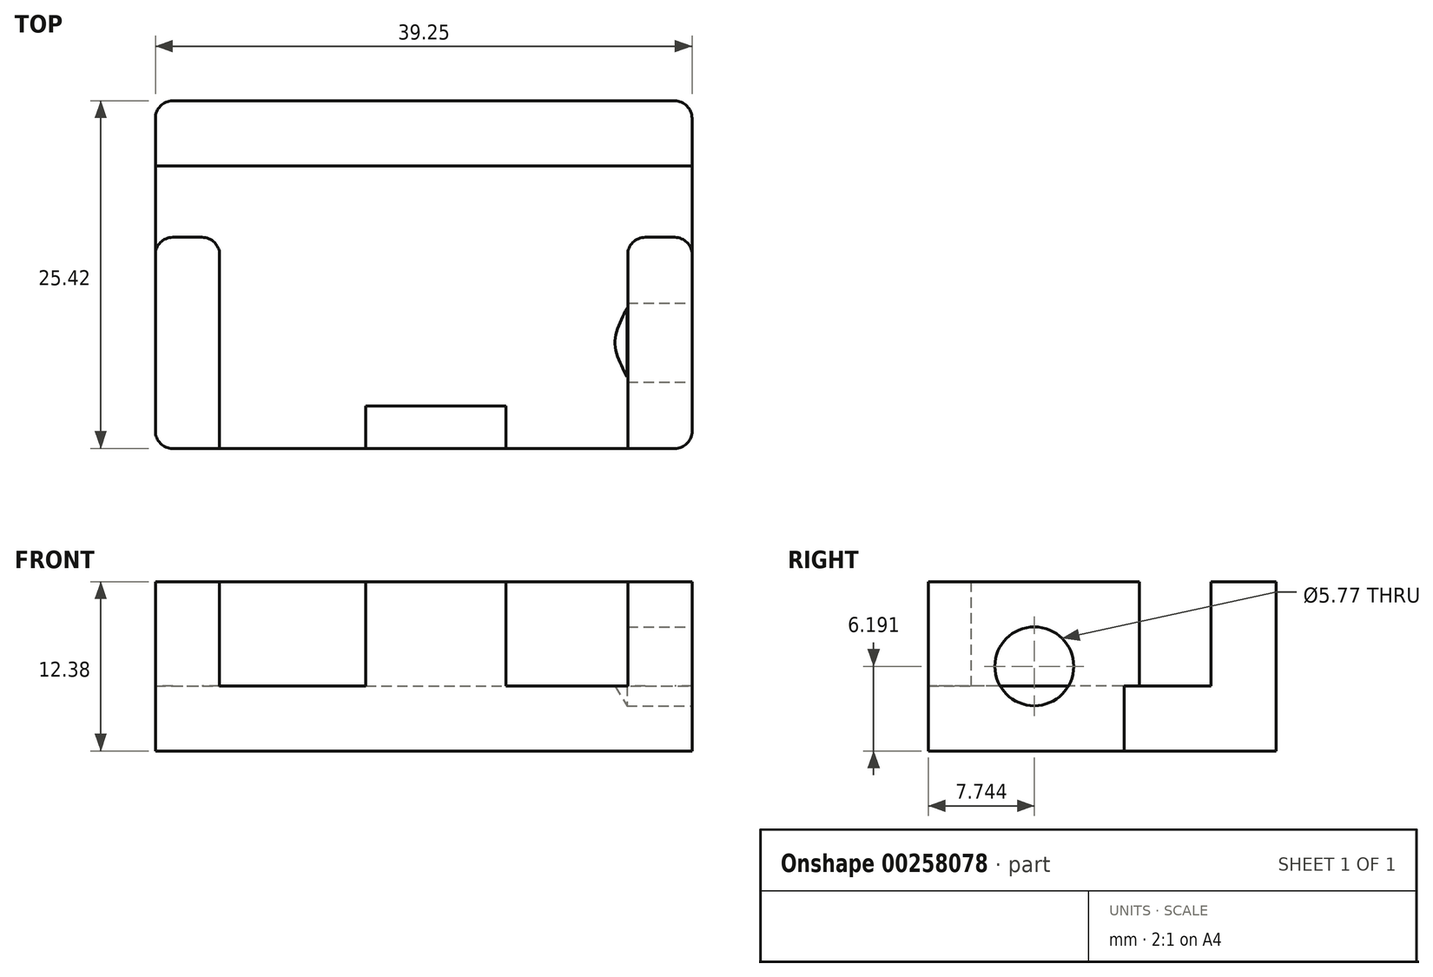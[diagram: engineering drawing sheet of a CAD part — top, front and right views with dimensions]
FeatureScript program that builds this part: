
annotation { "Feature Type Name" : "Feature", "Feature Type Description" : "" }
export const myFeature = defineFeature(function(context is Context, id is Id, definition is map)
    precondition{}
    {
        {
            var Q0;
            Q0=qCreatedBy(makeId("Top.planeOp"),FACE);
            var sketch = newSketch(context, id + "F0", { "sketchPlane" : qUnion([Q0])});
            skLineSegment(sketch, "E0.bottom", {"start": v(19.62, 12.71) * mm, "end": v(-19.62, 12.71) * mm});
            skLineSegment(sketch, "E0.top", {"start": v(19.62, -12.71) * mm, "end": v(-19.62, -12.71) * mm});
            skLineSegment(sketch, "E0.left", {"start": v(19.62, 12.71) * mm, "end": v(19.62, -12.71) * mm});
            skLineSegment(sketch, "E0.right", {"start": v(-19.62, 12.71) * mm, "end": v(-19.62, -12.71) * mm});
            skPoint(sketch, "E0.middle", {"position": v(0, 0) * mm});
            skSolve(sketch);
        }
        {
            var Q0;
            Q0=makeQuery(id+"F0.imprint","IMPRINT",FACE,{"disambiguationData":[TD([[makeQuery(id+"F0.imprint","IMPRINT",EDGE,{"derivedFrom":sQuery(id+"F0.wireOp",EDGE,"E0.bottom")}),1.0]])]});
            extrude(context, id + "F1", {"entities" : qUnion([Q0]), "depth" : 4.76 * mm});
        }
        {
            var Q0;
            Q0=makeQuery(id+"F1.opExtrude","CAP_FACE",FACE,{"disambiguationData":[OSD([sQuery(id+"F0.wireOp",EDGE,"E0.bottom"),sQuery(id+"F0.wireOp",EDGE,"E0.top"),sQuery(id+"F0.wireOp",EDGE,"E0.left"),sQuery(id+"F0.wireOp",EDGE,"E0.right")])],"isStart":false});
            var sketch = newSketch(context, id + "F2", { "sketchPlane" : qUnion([Q0])});
            skLineSegment(sketch, "E1.bottom", {"start": v(-19.62, 2.73) * mm, "end": v(-14.93, 2.73) * mm});
            skLineSegment(sketch, "E1.top", {"start": v(-19.62, -12.71) * mm, "end": v(-14.93, -12.71) * mm});
            skLineSegment(sketch, "E1.left", {"start": v(-19.62, 2.73) * mm, "end": v(-19.62, -12.71) * mm});
            skLineSegment(sketch, "E1.right", {"start": v(-14.93, 2.73) * mm, "end": v(-14.93, -12.71) * mm});
            skLineSegment(sketch, "E2.bottom", {"start": v(-19.62, 12.71) * mm, "end": v(19.62, 12.71) * mm});
            skLineSegment(sketch, "E2.top", {"start": v(-19.62, 7.95) * mm, "end": v(19.62, 7.95) * mm});
            skLineSegment(sketch, "E2.left", {"start": v(-19.62, 12.71) * mm, "end": v(-19.62, 7.95) * mm});
            skLineSegment(sketch, "E2.right", {"start": v(19.62, 12.71) * mm, "end": v(19.62, 7.95) * mm});
            skLineSegment(sketch, "E3.bottom", {"start": v(14.93, 2.73) * mm, "end": v(19.62, 2.73) * mm});
            skLineSegment(sketch, "E3.top", {"start": v(14.93, -12.71) * mm, "end": v(19.62, -12.71) * mm});
            skLineSegment(sketch, "E3.left", {"start": v(14.93, 2.73) * mm, "end": v(14.93, -12.71) * mm});
            skLineSegment(sketch, "E3.right", {"start": v(19.62, 2.73) * mm, "end": v(19.62, -12.71) * mm});
            skLineSegment(sketch, "E4.bottom", {"start": v(-4.23, -12.71) * mm, "end": v(6.01, -12.71) * mm});
            skLineSegment(sketch, "E4.top", {"start": v(-4.23, -9.6) * mm, "end": v(6.01, -9.6) * mm});
            skLineSegment(sketch, "E4.left", {"start": v(-4.23, -12.71) * mm, "end": v(-4.23, -9.6) * mm});
            skLineSegment(sketch, "E4.right", {"start": v(6.01, -12.71) * mm, "end": v(6.01, -9.6) * mm});
            skSolve(sketch);
        }
        {
            var Q0;
            Q0=makeQuery(id+"F2.imprint","IMPRINT",FACE,{"disambiguationData":[TD([[makeQuery(id+"F2.imprint","IMPRINT",EDGE,{"derivedFrom":sQuery(id+"F2.wireOp",EDGE,"E1.bottom")}),-1.0]])]});
            var Q1;
            Q1=makeQuery(id+"F2.imprint","IMPRINT",FACE,{"disambiguationData":[TD([[makeQuery(id+"F2.imprint","IMPRINT",EDGE,{"derivedFrom":sQuery(id+"F2.wireOp",EDGE,"E3.bottom")}),-1.0]])]});
            var Q2;
            Q2=makeQuery(id+"F2.imprint","IMPRINT",FACE,{"disambiguationData":[TD([[makeQuery(id+"F2.imprint","IMPRINT",EDGE,{"derivedFrom":sQuery(id+"F2.wireOp",EDGE,"E4.bottom")}),-1.0]])]});
            var Q3;
            Q3=makeQuery(id+"F2.imprint","IMPRINT",FACE,{"disambiguationData":[TD([[makeQuery(id+"F2.imprint","IMPRINT",EDGE,{"derivedFrom":sQuery(id+"F2.wireOp",EDGE,"E2.bottom")}),1.0]])]});
            extrude(context, id + "F3", {"entities" : qUnion([Q0, Q1, Q2, Q3]), "operationType" : NewBodyOperationType.ADD, "depth" : 7.62 * mm});
        }
        {
            var Q0;
            Q0=makeQuery(id+"F3.boolean.opBoolean","MERGE",FACE,{"derivedFrom":[makeQuery(id+"F1.opExtrude","SWEPT_FACE",FACE,{"disambiguationData":[OSD([sQuery(id+"F0.wireOp",EDGE,"E0.left")])]}),makeQuery(id+"F3.opExtrude","SWEPT_FACE",FACE,{"disambiguationData":[OSD([sQuery(id+"F2.wireOp",EDGE,"E2.right")])]}),makeQuery(id+"F3.opExtrude","SWEPT_FACE",FACE,{"disambiguationData":[OSD([sQuery(id+"F2.wireOp",EDGE,"E3.right")])]})]});
            var sketch = newSketch(context, id + "F4", { "sketchPlane" : qUnion([Q0])});
            skLineSegment(sketch, "E5.bottom", {"start": v(2.73, 12.38) * mm, "end": v(-12.71, 12.38) * mm});
            skLineSegment(sketch, "E5.top", {"start": v(2.73, 0) * mm, "end": v(-12.71, 0) * mm});
            skLineSegment(sketch, "E5.left", {"start": v(2.73, 12.38) * mm, "end": v(2.73, 0) * mm});
            skLineSegment(sketch, "E5.right", {"start": v(-12.71, 12.38) * mm, "end": v(-12.71, 0) * mm});
            skSolve(sketch);
        }
        {
            var Q0;
            {var subQ4=sQuery(id+"F4.wireOp",EDGE,"E5.bottom");Q0=makeQuery(id+"F4.imprint","IMPRINT",FACE,{"disambiguationData":[TD([[makeQuery(id+"F4.imprint","IMPRINT",EDGE,{"derivedFrom":subQ4}),1.0]])]});}
            extrude(context, id + "F5", {"entities" : qUnion([Q0]), "operationType" : NewBodyOperationType.ADD, "depth" : 3 / 406.4 * mm});
        }
        {
            var Q0;
            Q0=makeQuery(id+"F5.opExtrude","CAP_FACE",FACE,{"disambiguationData":[OSD([sQuery(id+"F4.wireOp",EDGE,"E5.bottom"),sQuery(id+"F4.wireOp",EDGE,"E5.top"),sQuery(id+"F4.wireOp",EDGE,"E5.left"),sQuery(id+"F4.wireOp",EDGE,"E5.right")])],"isStart":false});
            var sketch = newSketch(context, id + "F6", { "sketchPlane" : qUnion([Q0])});
            skPoint(sketch, "E6", {"position": v(-4.97, 6.2) * mm});
            skSolve(sketch);
        }
        {
            var Q0;
            Q0=sQuery(id+"F6.wireOp",VERTEX,"E6");
            var Q1;
            Q1=makeQuery(id+"F1.opExtrude","SWEPT_BODY",BODY,{"disambiguationData":[OSD([sQuery(id+"F0.wireOp",EDGE,"E0.bottom"),sQuery(id+"F0.wireOp",EDGE,"E0.top"),sQuery(id+"F0.wireOp",EDGE,"E0.left"),sQuery(id+"F0.wireOp",EDGE,"E0.right")])]});
            hole(context, id + "F7", {"style" : HoleStyle.SIMPLE, "endStyle" : HoleEndStyle.BLIND, "holeDiameter" : 5.77 * mm, "holeDepth" : 4.76 * mm, "tappedDepth" : 12.7 * mm, "tapClearance" : 3, "startFromSketch" : true, "locations" : qUnion([Q0]), "scope" : qUnion([Q1])});
        }
        {
            var Q0;
            Q0=makeQuery(id+"F3.opExtrude","SWEPT_EDGE",EDGE,{"disambiguationData":[OSD([sQuery(id+"F2.wireOp",EDGE,"E1.bottom"),sQuery(id+"F2.wireOp",EDGE,"E1.right")])]});
            var Q1;
            Q1=makeQuery(id+"F3.opExtrude","SWEPT_EDGE",EDGE,{"disambiguationData":[OSD([sQuery(id+"F2.wireOp",EDGE,"E3.bottom"),sQuery(id+"F2.wireOp",EDGE,"E3.left")])]});
            var Q2;
            Q2=makeQuery(id+"F3.boolean.opBoolean","MERGE",EDGE,{"derivedFrom":[makeQuery(id+"F1.opExtrude","SWEPT_EDGE",EDGE,{"disambiguationData":[OSD([sQuery(id+"F0.wireOp",EDGE,"E0.top"),sQuery(id+"F0.wireOp",EDGE,"E0.right")])]}),makeQuery(id+"F3.opExtrude","SWEPT_EDGE",EDGE,{"disambiguationData":[OSD([sQuery(id+"F2.wireOp",EDGE,"E1.top"),sQuery(id+"F2.wireOp",EDGE,"E1.left")])]})]});
            var Q3;
            Q3=makeQuery(id+"F5.opExtrude","CAP_EDGE",EDGE,{"disambiguationData":[OSD([sQuery(id+"F4.wireOp",EDGE,"E5.right")])],"isStart":false});
            var Q4;
            Q4=makeQuery(id+"F5.opExtrude","CAP_EDGE",EDGE,{"disambiguationData":[OSD([sQuery(id+"F4.wireOp",EDGE,"E5.left")])],"isStart":false});
            var Q5;
            Q5=makeQuery(id+"F3.boolean.opBoolean","MERGE",EDGE,{"derivedFrom":[makeQuery(id+"F1.opExtrude","SWEPT_EDGE",EDGE,{"disambiguationData":[OSD([sQuery(id+"F0.wireOp",EDGE,"E0.bottom"),sQuery(id+"F0.wireOp",EDGE,"E0.left")])]}),makeQuery(id+"F3.opExtrude","SWEPT_EDGE",EDGE,{"disambiguationData":[OSD([sQuery(id+"F2.wireOp",EDGE,"E2.bottom"),sQuery(id+"F2.wireOp",EDGE,"E2.right")])]})]});
            var Q6;
            Q6=makeQuery(id+"F3.boolean.opBoolean","MERGE",EDGE,{"derivedFrom":[makeQuery(id+"F1.opExtrude","SWEPT_EDGE",EDGE,{"disambiguationData":[OSD([sQuery(id+"F0.wireOp",EDGE,"E0.bottom"),sQuery(id+"F0.wireOp",EDGE,"E0.right")])]}),makeQuery(id+"F3.opExtrude","SWEPT_EDGE",EDGE,{"disambiguationData":[OSD([sQuery(id+"F2.wireOp",EDGE,"E2.bottom"),sQuery(id+"F2.wireOp",EDGE,"E2.left")])]})]});
            var Q7;
            Q7=makeQuery(id+"F3.opExtrude","SWEPT_EDGE",EDGE,{"disambiguationData":[OSD([sQuery(id+"F0.wireOp",EDGE,"E0.right"),sQuery(id+"F2.wireOp",EDGE,"E1.bottom"),sQuery(id+"F2.wireOp",EDGE,"E1.left")])]});
            fillet(context, id + "F8", {"entities" : qUnion([Q0, Q1, Q2, Q3, Q4, Q5, Q6, Q7]), "radius" : 1.27 * mm, "tangentPropagation" : true, "allowEdgeOverflow" : false});
        }
    });
